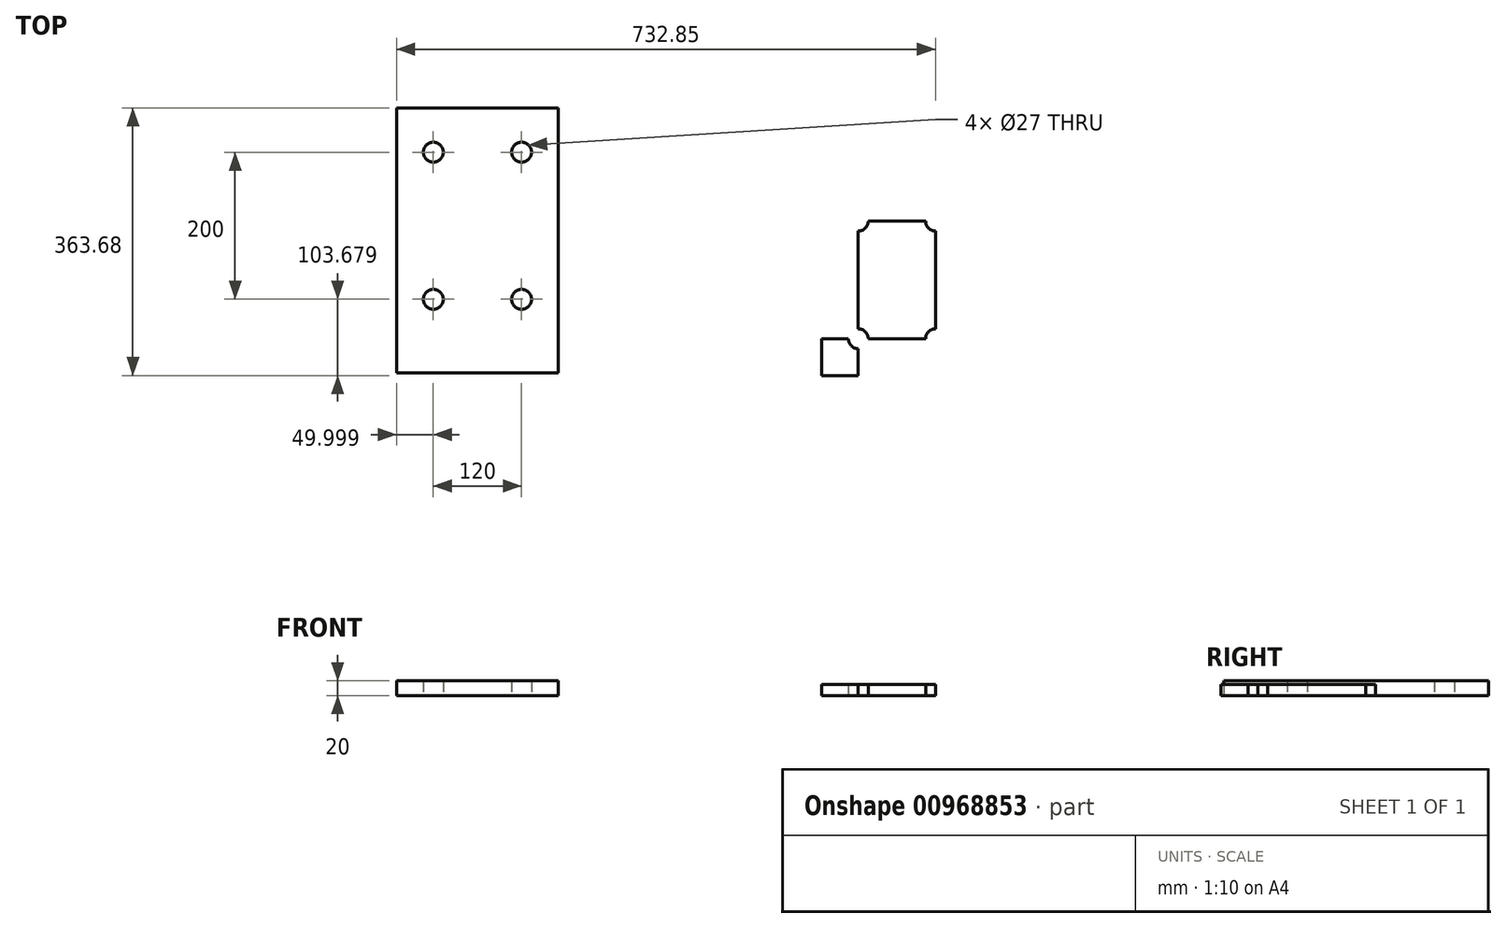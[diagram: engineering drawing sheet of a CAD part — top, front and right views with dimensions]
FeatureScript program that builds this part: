
annotation { "Feature Type Name" : "Feature", "Feature Type Description" : "" }
export const myFeature = defineFeature(function(context is Context, id is Id, definition is map)
    precondition{}
    {
        {
            var Q0;
            Q0=qCreatedBy(makeId("Top.planeOp"),FACE);
            var sketch = newSketch(context, id + "F0", { "sketchPlane" : qUnion([Q0])});
            skLineSegment(sketch, "E0.bottom", {"start": v(-65.44, 34.42) * mm, "end": v(154.56, 34.42) * mm});
            skLineSegment(sketch, "E0.top", {"start": v(-65.44, 394.42) * mm, "end": v(154.56, 394.42) * mm});
            skLineSegment(sketch, "E0.left", {"start": v(-65.44, 34.42) * mm, "end": v(-65.44, 394.42) * mm});
            skLineSegment(sketch, "E0.right", {"start": v(154.56, 34.42) * mm, "end": v(154.56, 394.42) * mm});
            skLineSegment(sketch, "E1.bottom", {"start": v(-65.44, 34.42) * mm, "end": v(-15.44, 34.42) * mm});
            skLineSegment(sketch, "E2.bottom", {"start": v(-15.44, 134.42) * mm, "end": v(104.56, 134.42) * mm});
            skLineSegment(sketch, "E2.top", {"start": v(-15.44, 334.42) * mm, "end": v(104.56, 334.42) * mm});
            skLineSegment(sketch, "E2.left", {"start": v(-15.44, 134.42) * mm, "end": v(-15.44, 334.42) * mm});
            skLineSegment(sketch, "E2.right", {"start": v(104.56, 134.42) * mm, "end": v(104.56, 334.42) * mm});
            skCircle(sketch, "E3", {"center": v(-15.44, 134.42) * mm, "radius": 13.5 * mm});
            skCircle(sketch, "E4", {"center": v(104.56, 134.42) * mm, "radius": 13.5 * mm});
            skCircle(sketch, "E5", {"center": v(104.56, 334.42) * mm, "radius": 13.5 * mm});
            skCircle(sketch, "E6", {"center": v(-15.44, 334.42) * mm, "radius": 13.5 * mm});
            skSolve(sketch);
        }
        {
            var Q0;
            {var subQ5=sQuery(id+"F0.wireOp",EDGE,"E3");var subQ13=sQuery(id+"F0.wireOp",EDGE,"E2.bottom");var subQ14=makeQuery(id+"F0.imprint","INTERSECT",VERTEX,{"derivedFrom":[subQ13,subQ5]});Q0=makeQuery(id+"F0.imprint","IMPRINT",FACE,{"disambiguationData":[TD([[makeQuery(id+"F0.imprint","IMPRINT",EDGE,{"disambiguationData":[TD([[subQ14,-1.0]])],"derivedFrom":subQ13}),1.0]])]});}
            var Q1;
            Q1=makeQuery(id+"F0.imprint","IMPRINT",FACE,{"disambiguationData":[TD([[makeQuery(id+"F0.imprint","IMPRINT",EDGE,{"derivedFrom":sQuery(id+"F0.wireOp",EDGE,"E0.bottom")}),1.0]])]});
            extrude(context, id + "F1", {"entities" : qUnion([Q0, Q1]), "depth" : 20 * mm, "offsetDistance" : 25 * mm});
        }
        {
            var Q0;
            Q0=qCreatedBy(makeId("Top.planeOp"),FACE);
            var sketch = newSketch(context, id + "F2", { "sketchPlane" : qUnion([Q0])});
            skLineSegment(sketch, "E7.bottom", {"start": v(206.66, 32.47) * mm, "end": v(406.66, 32.47) * mm});
            skLineSegment(sketch, "E7.top", {"start": v(206.66, 232.47) * mm, "end": v(406.66, 232.47) * mm});
            skLineSegment(sketch, "E7.left", {"start": v(206.66, 32.47) * mm, "end": v(206.66, 232.47) * mm});
            skLineSegment(sketch, "E7.right", {"start": v(406.66, 32.47) * mm, "end": v(406.66, 232.47) * mm});
            skLineSegment(sketch, "E8", {"start": v(206.66, 232.47) * mm, "end": v(206.66, 182.47) * mm});
            skLineSegment(sketch, "E9", {"start": v(406.66, 32.47) * mm, "end": v(356.66, 32.47) * mm});
            skLineSegment(sketch, "E10", {"start": v(356.66, 32.47) * mm, "end": v(206.66, 182.47) * mm});
            skCircle(sketch, "E11", {"center": v(406.66, 232.47) * mm, "radius": 40 * mm});
            skLineSegment(sketch, "E12.bottom", {"start": v(512.41, 30.74) * mm, "end": v(732.41, 30.74) * mm});
            skLineSegment(sketch, "E12.top", {"start": v(512.41, 290.74) * mm, "end": v(732.41, 290.74) * mm});
            skLineSegment(sketch, "E12.left", {"start": v(512.41, 30.74) * mm, "end": v(512.41, 290.74) * mm});
            skLineSegment(sketch, "E12.right", {"start": v(732.41, 30.74) * mm, "end": v(732.41, 290.74) * mm});
            skLineSegment(sketch, "E13.bottom", {"start": v(512.41, 30.74) * mm, "end": v(562.41, 30.74) * mm});
            skLineSegment(sketch, "E13.top", {"start": v(512.41, 80.74) * mm, "end": v(562.41, 80.74) * mm});
            skLineSegment(sketch, "E13.left", {"start": v(512.41, 30.74) * mm, "end": v(512.41, 80.74) * mm});
            skLineSegment(sketch, "E13.right", {"start": v(562.41, 30.74) * mm, "end": v(562.41, 80.74) * mm});
            skLineSegment(sketch, "E14.bottom", {"start": v(562.41, 80.74) * mm, "end": v(667.41, 80.74) * mm});
            skLineSegment(sketch, "E14.top", {"start": v(562.41, 240.74) * mm, "end": v(667.41, 240.74) * mm});
            skLineSegment(sketch, "E14.left", {"start": v(562.41, 80.74) * mm, "end": v(562.41, 240.74) * mm});
            skLineSegment(sketch, "E14.right", {"start": v(667.41, 80.74) * mm, "end": v(667.41, 240.74) * mm});
            skCircle(sketch, "E15", {"center": v(562.41, 80.74) * mm, "radius": 13.5 * mm});
            skCircle(sketch, "E16", {"center": v(667.41, 80.74) * mm, "radius": 13.5 * mm});
            skCircle(sketch, "E17", {"center": v(667.41, 240.74) * mm, "radius": 13.5 * mm});
            skCircle(sketch, "E18", {"center": v(562.41, 240.74) * mm, "radius": 13.5 * mm});
            skSolve(sketch);
        }
        {
            var Q0;
            {var subQ4=sQuery(id+"F2.wireOp",EDGE,"E8");Q0=makeQuery(id+"F2.imprint","IMPRINT",FACE,{"disambiguationData":[TD([[makeQuery(id+"F2.imprint","IMPRINT",EDGE,{"derivedFrom":subQ4}),1.0]])]});}
            var Q1;
            {var subQ10=sQuery(id+"F2.wireOp",EDGE,"E15");var subQ13=sQuery(id+"F2.wireOp",EDGE,"E14.bottom");var subQ14=makeQuery(id+"F2.imprint","INTERSECT",VERTEX,{"derivedFrom":[subQ13,subQ10]});Q1=makeQuery(id+"F2.imprint","IMPRINT",FACE,{"disambiguationData":[TD([[makeQuery(id+"F2.imprint","IMPRINT",EDGE,{"disambiguationData":[TD([[subQ14,-1.0]])],"derivedFrom":subQ13}),1.0]])]});}
            var Q2;
            {var subQ11=sQuery(id+"F2.wireOp",EDGE,"E12.bottom");Q2=makeQuery(id+"F2.imprint","IMPRINT",FACE,{"disambiguationData":[TD([[makeQuery(id+"F2.imprint","IMPRINT",EDGE,{"derivedFrom":subQ11}),1.0]])]});}
            var Q3;
            {var subQ1=sQuery(id+"F2.wireOp",EDGE,"E13.bottom");Q3=makeQuery(id+"F2.imprint","IMPRINT",FACE,{"disambiguationData":[TD([[makeQuery(id+"F2.imprint","IMPRINT",EDGE,{"derivedFrom":subQ1}),1.0]])]});}
            extrude(context, id + "F3", {"entities" : qUnion([Q0, Q1, Q2, Q3]), "depth" : 15 * mm, "offsetDistance" : 25 * mm});
        }
    });
